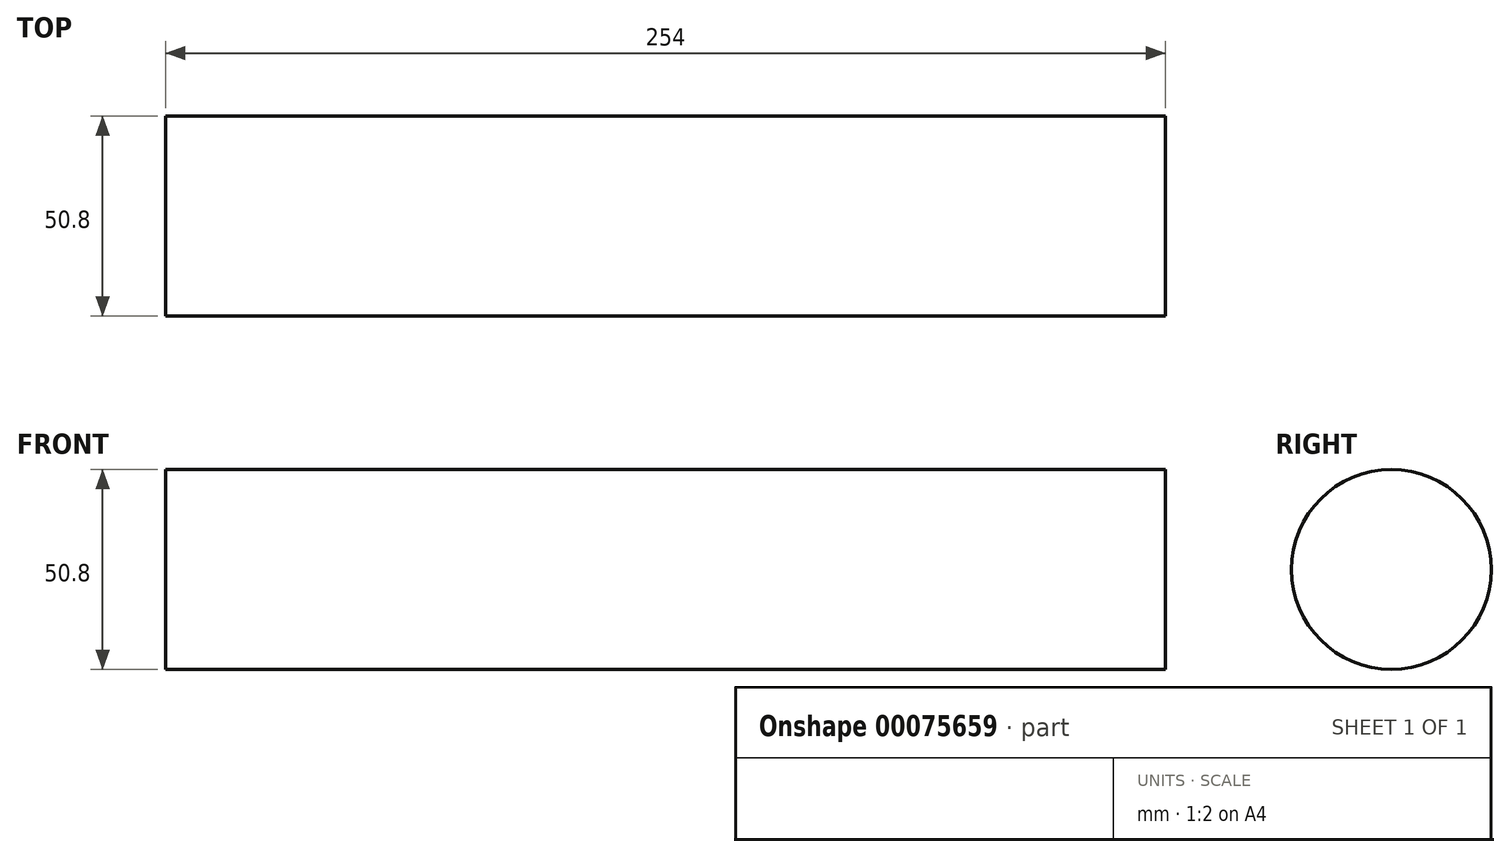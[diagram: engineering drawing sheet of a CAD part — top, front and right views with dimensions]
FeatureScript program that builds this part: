
annotation { "Feature Type Name" : "Feature", "Feature Type Description" : "" }
export const myFeature = defineFeature(function(context is Context, id is Id, definition is map)
    precondition{}
    {
        {
            var Q0;
            Q0=qCreatedBy(makeId("Front.planeOp"),FACE);
            var sketch = newSketch(context, id + "F0", { "sketchPlane" : qUnion([Q0])});
            skLineSegment(sketch, "E0.bottom", {"start": v(-57.72, 36.58) * mm, "end": v(196.28, 36.58) * mm});
            skLineSegment(sketch, "E0.top", {"start": v(-57.72, 11.18) * mm, "end": v(196.28, 11.18) * mm});
            skLineSegment(sketch, "E0.left", {"start": v(-57.72, 36.58) * mm, "end": v(-57.72, 11.18) * mm});
            skLineSegment(sketch, "E0.right", {"start": v(196.28, 36.58) * mm, "end": v(196.28, 11.18) * mm});
            skSolve(sketch);
        }
        {
            var Q0;
            Q0=makeQuery(id+"F0.imprint","IMPRINT",FACE,{"disambiguationData":[TD([[makeQuery(id+"F0.imprint","IMPRINT",EDGE,{"derivedFrom":sQuery(id+"F0.wireOp",EDGE,"E0.bottom")}),-1.0]])]});
            var Q1;
            Q1=sQuery(id+"F0.wireOp",EDGE,"E0.top");
            revolve(context, id + "F1", {"entities" : qUnion([Q0]), "axis" : qUnion([Q1]), "revolveType" : RevolveType.FULL});
        }
    });
